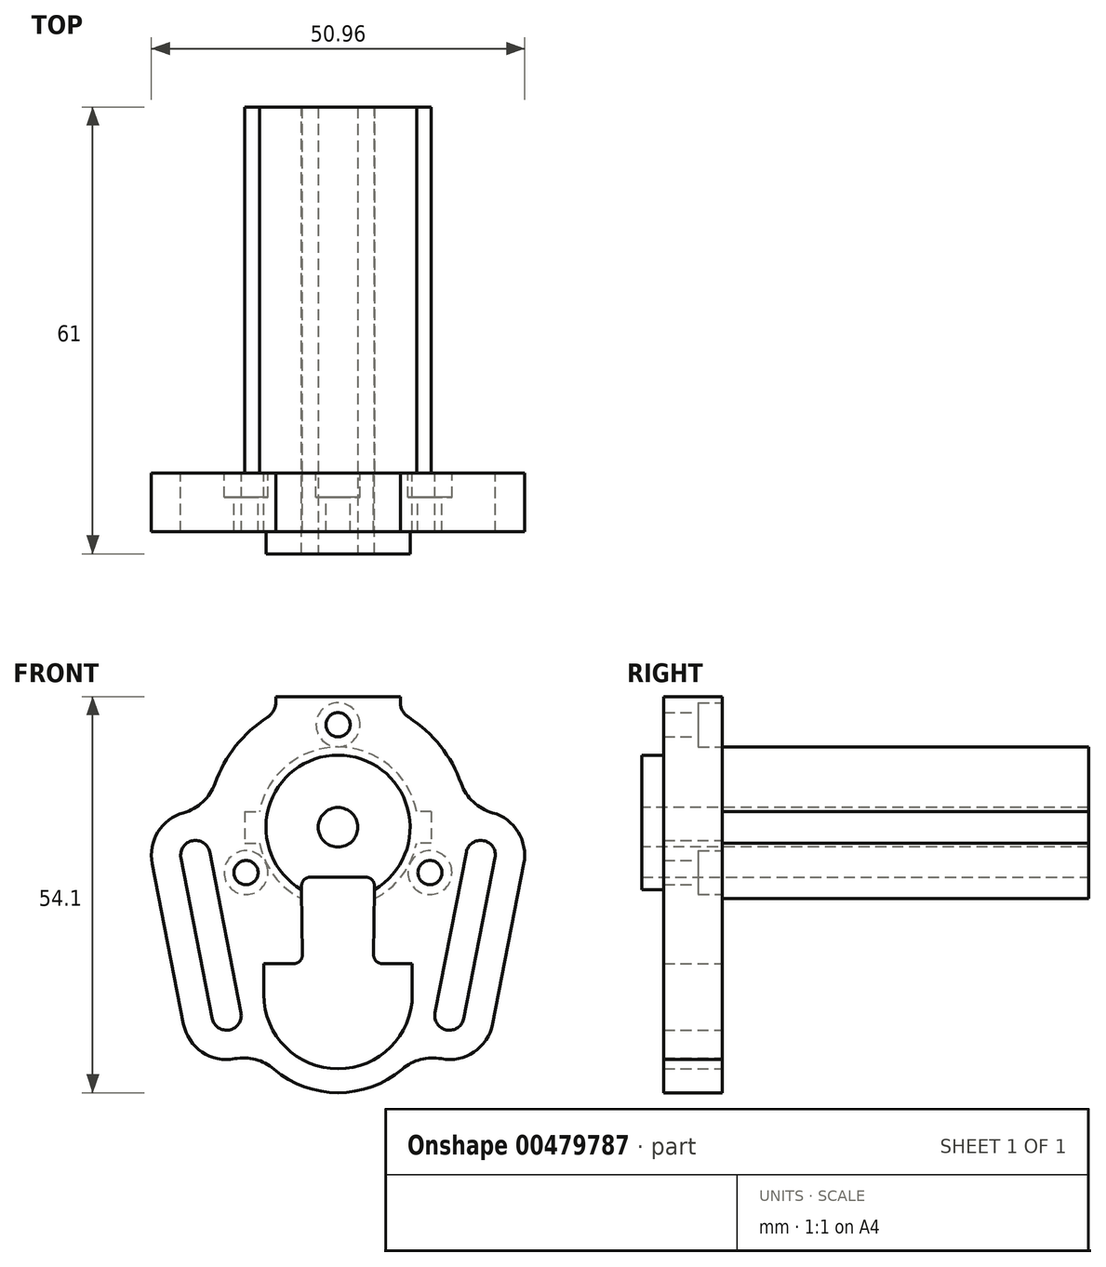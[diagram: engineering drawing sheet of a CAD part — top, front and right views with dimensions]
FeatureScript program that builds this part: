
annotation { "Feature Type Name" : "Feature", "Feature Type Description" : "" }
export const myFeature = defineFeature(function(context is Context, id is Id, definition is map)
    precondition{}
    {
        {
            var Q0;
            Q0=qCreatedBy(makeId("Front.planeOp"),FACE);
            var sketch = newSketch(context, id + "F0", { "sketchPlane" : qUnion([Q0])});
            skArc(sketch, "E0", {"start": v(16.82, 5.97) * mm, "mid": v(13.99, 11.1) * mm, "end": v(9.65, 15.02) * mm});
            skLineSegment(sketch, "E1", {"start": v(0, 17.85) * mm, "end": v(0, -22.75) * mm, "construction": true});
            skArc(sketch, "E2", {"start": v(-8.77, -33.02) * mm, "mid": v(0, -36.25) * mm, "end": v(8.77, -33.02) * mm});
            skLineSegment(sketch, "E3", {"start": v(13.25, -25.33) * mm, "end": v(17.52, -3.41) * mm});
            skLineSegment(sketch, "E4", {"start": v(-17.52, -3.41) * mm, "end": v(-13.25, -25.33) * mm});
            skArc(sketch, "E5", {"start": v(-17.52, -3.41) * mm, "mid": v(-19.87, -1.83) * mm, "end": v(-21.45, -4.18) * mm});
            skArc(sketch, "E6", {"start": v(-13.25, -25.33) * mm, "mid": v(-14.83, -27.68) * mm, "end": v(-17.18, -26.1) * mm});
            skArc(sketch, "E7", {"start": v(13.25, -25.33) * mm, "mid": v(14.83, -27.68) * mm, "end": v(17.18, -26.1) * mm});
            skArc(sketch, "E8", {"start": v(17.52, -3.41) * mm, "mid": v(19.87, -1.83) * mm, "end": v(21.45, -4.18) * mm});
            skLineSegment(sketch, "E9", {"start": v(17.18, -26.1) * mm, "end": v(21.45, -4.18) * mm});
            skLineSegment(sketch, "E10", {"start": v(-21.45, -4.18) * mm, "end": v(-17.18, -26.1) * mm});
            skArc(sketch, "E11.0", {"start": v(-14.09, -31.6) * mm, "mid": v(-18.58, -30.68) * mm, "end": v(-21.1, -26.86) * mm});
            skLineSegment(sketch, "E11.1", {"start": v(-25.37, -4.94) * mm, "end": v(-21.1, -26.86) * mm});
            skArc(sketch, "E11.2", {"start": v(-21.1, 1.98) * mm, "mid": v(-24.59, -0.64) * mm, "end": v(-25.37, -4.94) * mm});
            skArc(sketch, "E12.0", {"start": v(14.09, -31.6) * mm, "mid": v(18.58, -30.68) * mm, "end": v(21.1, -26.86) * mm});
            skLineSegment(sketch, "E12.1", {"start": v(21.1, -26.86) * mm, "end": v(25.37, -4.94) * mm});
            skArc(sketch, "E12.2", {"start": v(21.1, 1.98) * mm, "mid": v(24.59, -0.64) * mm, "end": v(25.37, -4.94) * mm});
            skPoint(sketch, "E13.visualSharp", {"position": v(-17.74, 1.95) * mm});
            skArc(sketch, "E13.filletArc", {"start": v(-21.1, 1.98) * mm, "mid": v(-18.47, 3.46) * mm, "end": v(-16.82, 5.97) * mm});
            skPoint(sketch, "E14.visualSharp", {"position": v(17.74, 1.95) * mm});
            skArc(sketch, "E14.filletArc", {"start": v(16.82, 5.97) * mm, "mid": v(18.47, 3.46) * mm, "end": v(21.1, 1.98) * mm});
            skPoint(sketch, "E15.visualSharp", {"position": v(-11.25, -30.22) * mm});
            skArc(sketch, "E15.filletArc", {"start": v(-8.77, -33.02) * mm, "mid": v(-11.27, -31.7) * mm, "end": v(-14.09, -31.6) * mm});
            skPoint(sketch, "E16.visualSharp", {"position": v(11.25, -30.22) * mm});
            skArc(sketch, "E16.filletArc", {"start": v(14.09, -31.6) * mm, "mid": v(11.27, -31.7) * mm, "end": v(8.77, -33.02) * mm});
            skLineSegment(sketch, "E17", {"start": v(0, 17.85) * mm, "end": v(-8.5, 17.85) * mm});
            skLineSegment(sketch, "E18.MirrorCS", {"start": v(0, 17.85) * mm, "end": v(8.5, 17.85) * mm});
            skLineSegment(sketch, "E19", {"start": v(-8.5, 17.85) * mm, "end": v(-8.5, 17.12) * mm});
            skLineSegment(sketch, "E20", {"start": v(8.5, 17.85) * mm, "end": v(8.5, 17.12) * mm});
            skArc(sketch, "E21.trimOffspring", {"start": v(-9.65, 15.02) * mm, "mid": v(-13.99, 11.1) * mm, "end": v(-16.82, 5.97) * mm});
            skPoint(sketch, "E22.visualSharp", {"position": v(-8.5, 15.7) * mm});
            skArc(sketch, "E22.filletArc", {"start": v(-9.65, 15.02) * mm, "mid": v(-8.8, 15.92) * mm, "end": v(-8.5, 17.12) * mm});
            skPoint(sketch, "E23.visualSharp", {"position": v(8.5, 15.7) * mm});
            skArc(sketch, "E23.filletArc", {"start": v(8.5, 17.12) * mm, "mid": v(8.8, 15.92) * mm, "end": v(9.65, 15.02) * mm});
            skSolve(sketch);
        }
        {
            var Q0;
            Q0=makeQuery(id+"F0.imprint","IMPRINT",FACE,{"disambiguationData":[TD([[makeQuery(id+"F0.imprint","IMPRINT",EDGE,{"derivedFrom":sQuery(id+"F0.wireOp",EDGE,"E0")}),1.0]])]});
            extrude(context, id + "F1", {"entities" : qUnion([Q0]), "depth" : 8 * mm});
        }
        {
            var Q0;
            Q0=makeQuery(id+"F1.opExtrude","CAP_FACE",FACE,{"disambiguationData":[OSD([sQuery(id+"F0.wireOp",EDGE,"E0"),sQuery(id+"F0.wireOp",EDGE,"E2"),sQuery(id+"F0.wireOp",EDGE,"E3"),sQuery(id+"F0.wireOp",EDGE,"E4"),sQuery(id+"F0.wireOp",EDGE,"E5"),sQuery(id+"F0.wireOp",EDGE,"E6"),sQuery(id+"F0.wireOp",EDGE,"E7"),sQuery(id+"F0.wireOp",EDGE,"E8"),sQuery(id+"F0.wireOp",EDGE,"E9"),sQuery(id+"F0.wireOp",EDGE,"E10"),sQuery(id+"F0.wireOp",EDGE,"E11.0"),sQuery(id+"F0.wireOp",EDGE,"E11.1"),sQuery(id+"F0.wireOp",EDGE,"E11.2"),sQuery(id+"F0.wireOp",EDGE,"E12.0"),sQuery(id+"F0.wireOp",EDGE,"E12.1"),sQuery(id+"F0.wireOp",EDGE,"E12.2"),sQuery(id+"F0.wireOp",EDGE,"E13.filletArc"),sQuery(id+"F0.wireOp",EDGE,"E14.filletArc"),sQuery(id+"F0.wireOp",EDGE,"E15.filletArc"),sQuery(id+"F0.wireOp",EDGE,"E16.filletArc"),sQuery(id+"F0.wireOp",EDGE,"E17"),sQuery(id+"F0.wireOp",EDGE,"E18.MirrorCS"),sQuery(id+"F0.wireOp",EDGE,"E19"),sQuery(id+"F0.wireOp",EDGE,"E20"),sQuery(id+"F0.wireOp",EDGE,"E21.trimOffspring"),sQuery(id+"F0.wireOp",EDGE,"E22.filletArc"),sQuery(id+"F0.wireOp",EDGE,"E23.filletArc")])],"isStart":false});
            var sketch = newSketch(context, id + "F2", { "sketchPlane" : qUnion([Q0])});
            skCircle(sketch, "E24", {"center": v(0, 0) * mm, "radius": 9.85 * mm});
            skSolve(sketch);
        }
        {
            var Q0;
            Q0=makeQuery(id+"F2.imprint","IMPRINT",FACE,{"disambiguationData":[TD([[makeQuery(id+"F2.imprint","IMPRINT",EDGE,{"derivedFrom":sQuery(id+"F2.wireOp",EDGE,"E24")}),1.0]])]});
            extrude(context, id + "F3", {"entities" : qUnion([Q0]), "operationType" : NewBodyOperationType.ADD, "depth" : 3 * mm});
        }
        {
            var Q0;
            Q0=makeQuery(id+"F1.opExtrude","CAP_FACE",FACE,{"disambiguationData":[OSD([sQuery(id+"F0.wireOp",EDGE,"E0"),sQuery(id+"F0.wireOp",EDGE,"E2"),sQuery(id+"F0.wireOp",EDGE,"E3"),sQuery(id+"F0.wireOp",EDGE,"E4"),sQuery(id+"F0.wireOp",EDGE,"E5"),sQuery(id+"F0.wireOp",EDGE,"E6"),sQuery(id+"F0.wireOp",EDGE,"E7"),sQuery(id+"F0.wireOp",EDGE,"E8"),sQuery(id+"F0.wireOp",EDGE,"E9"),sQuery(id+"F0.wireOp",EDGE,"E10"),sQuery(id+"F0.wireOp",EDGE,"E11.0"),sQuery(id+"F0.wireOp",EDGE,"E11.1"),sQuery(id+"F0.wireOp",EDGE,"E11.2"),sQuery(id+"F0.wireOp",EDGE,"E12.0"),sQuery(id+"F0.wireOp",EDGE,"E12.1"),sQuery(id+"F0.wireOp",EDGE,"E12.2"),sQuery(id+"F0.wireOp",EDGE,"E13.filletArc"),sQuery(id+"F0.wireOp",EDGE,"E14.filletArc"),sQuery(id+"F0.wireOp",EDGE,"E15.filletArc"),sQuery(id+"F0.wireOp",EDGE,"E16.filletArc"),sQuery(id+"F0.wireOp",EDGE,"E17"),sQuery(id+"F0.wireOp",EDGE,"E18.MirrorCS"),sQuery(id+"F0.wireOp",EDGE,"E19"),sQuery(id+"F0.wireOp",EDGE,"E20"),sQuery(id+"F0.wireOp",EDGE,"E21.trimOffspring"),sQuery(id+"F0.wireOp",EDGE,"E22.filletArc"),sQuery(id+"F0.wireOp",EDGE,"E23.filletArc")])],"isStart":true});
            var sketch = newSketch(context, id + "F4", { "sketchPlane" : qUnion([Q0])});
            skLineSegment(sketch, "E25", {"start": v(0, 0) * mm, "end": v(0, 2.17) * mm, "construction": true});
            skLineSegment(sketch, "E26", {"start": v(0, 2.17) * mm, "end": v(12.73, 2.17) * mm, "construction": true});
            skLineSegment(sketch, "E27.MirrorCS", {"start": v(0, 2.17) * mm, "end": v(-12.73, 2.17) * mm, "construction": true});
            skArc(sketch, "E28", {"start": v(-10.73, -2.17) * mm, "mid": v(0, -10.95) * mm, "end": v(10.73, -2.17) * mm});
            skLineSegment(sketch, "E29", {"start": v(-12.73, 2.17) * mm, "end": v(-10.73, 2.17) * mm});
            skLineSegment(sketch, "E30", {"start": v(-12.73, 2.17) * mm, "end": v(-12.73, -2.17) * mm});
            skLineSegment(sketch, "E31", {"start": v(0, 0) * mm, "end": v(4.4, 0) * mm, "construction": true});
            skLineSegment(sketch, "E32.MirrorCS", {"start": v(-12.73, -2.17) * mm, "end": v(-10.73, -2.17) * mm});
            skLineSegment(sketch, "E33.MirrorCS", {"start": v(12.73, -2.17) * mm, "end": v(10.73, -2.17) * mm});
            skLineSegment(sketch, "E34.MirrorCS", {"start": v(12.73, 2.17) * mm, "end": v(12.73, -2.17) * mm});
            skLineSegment(sketch, "E35.MirrorCS", {"start": v(12.73, 2.17) * mm, "end": v(10.73, 2.17) * mm});
            skArc(sketch, "E36.trimOffspring", {"start": v(10.73, 2.17) * mm, "mid": v(0, 10.95) * mm, "end": v(-10.73, 2.17) * mm});
            skSolve(sketch);
        }
        {
            var Q0;
            Q0 = qSketchRegion(id + "F4", true);
            extrude(context, id + "F5", {"entities" : qUnion([Q0]), "operationType" : NewBodyOperationType.ADD, "depth" : 50 * mm});
        }
        {
            var Q0;
            Q0=makeQuery(id+"F3.opExtrude","CAP_FACE",FACE,{"disambiguationData":[OSD([sQuery(id+"F2.wireOp",EDGE,"E24")])],"isStart":false});
            var sketch = newSketch(context, id + "F6", { "sketchPlane" : qUnion([Q0])});
            skCircle(sketch, "E37", {"center": v(0, 0) * mm, "radius": 2.7 * mm});
            skSolve(sketch);
        }
        {
            var Q0;
            Q0 = qSketchRegion(id + "F6", true);
            var Q1;
            Q1=makeQuery(id+"F6.imprint","IMPRINT",FACE,{"disambiguationData":[TD([[makeQuery(id+"F6.imprint","IMPRINT",EDGE,{"derivedFrom":sQuery(id+"F6.wireOp",EDGE,"E37")}),1.0]])]});
            extrude(context, id + "F7", {"entities" : qUnion([Q0, Q1]), "operationType" : NewBodyOperationType.REMOVE, "endBound" : BoundingType.UP_TO_NEXT, "oppositeDirection" : true, "depth" : 25 * mm});
        }
        {
            var Q0;
            Q0=makeQuery(id+"F4.imprint","IMPRINT",FACE,{"disambiguationData":[TD([[makeQuery(id+"F4.imprint","IMPRINT",EDGE,{"derivedFrom":sQuery(id+"F4.wireOp",EDGE,"E28")}),-1.0]])]});
            var sketch = newSketch(context, id + "F8", { "sketchPlane" : qUnion([Q0])});
            skCircle(sketch, "E38", {"center": v(0, 0) * mm, "radius": 14 * mm, "construction": true});
            skLineSegment(sketch, "E39", {"start": v(0, 0) * mm, "end": v(0, 22.33) * mm, "construction": true});
            skLineSegment(sketch, "E40", {"start": v(0, 0) * mm, "end": v(-15.1, -7.44) * mm, "construction": true});
            skLineSegment(sketch, "E41.MirrorCS", {"start": v(0, 0) * mm, "end": v(15.1, -7.44) * mm, "construction": true});
            skCircle(sketch, "E42", {"center": v(0, 14) * mm, "radius": 1.65 * mm});
            skCircle(sketch, "E43", {"center": v(-12.56, -6.2) * mm, "radius": 1.65 * mm});
            skCircle(sketch, "E44", {"center": v(12.56, -6.2) * mm, "radius": 1.65 * mm});
            skCircle(sketch, "E45", {"center": v(0, 14) * mm, "radius": 3 * mm});
            skCircle(sketch, "E46", {"center": v(-12.56, -6.2) * mm, "radius": 3 * mm});
            skCircle(sketch, "E47", {"center": v(12.56, -6.2) * mm, "radius": 3 * mm});
            skSolve(sketch);
        }
        {
            var Q0;
            Q0 = qSketchRegion(id + "F8", true);
            extrude(context, id + "F9", {"entities" : qUnion([Q0]), "operationType" : NewBodyOperationType.REMOVE, "oppositeDirection" : true, "depth" : 3.3 * mm});
        }
        {
            var Q0;
            Q0=makeQuery(id+"F9.boolean.opBoolean","SPLIT",FACE,{"disambiguationData":[TD([makeQuery(id+"F9.opExtrude","SWEPT_FACE",FACE,{"disambiguationData":[OSD([sQuery(id+"F8.wireOp",EDGE,"E44")])]})])],"derivedFrom":makeQuery(id+"F1.opExtrude","CAP_FACE",FACE,{"disambiguationData":[OSD([sQuery(id+"F0.wireOp",EDGE,"E0"),sQuery(id+"F0.wireOp",EDGE,"E2"),sQuery(id+"F0.wireOp",EDGE,"E3"),sQuery(id+"F0.wireOp",EDGE,"E4"),sQuery(id+"F0.wireOp",EDGE,"E5"),sQuery(id+"F0.wireOp",EDGE,"E6"),sQuery(id+"F0.wireOp",EDGE,"E7"),sQuery(id+"F0.wireOp",EDGE,"E8"),sQuery(id+"F0.wireOp",EDGE,"E9"),sQuery(id+"F0.wireOp",EDGE,"E10"),sQuery(id+"F0.wireOp",EDGE,"E11.0"),sQuery(id+"F0.wireOp",EDGE,"E11.1"),sQuery(id+"F0.wireOp",EDGE,"E11.2"),sQuery(id+"F0.wireOp",EDGE,"E12.0"),sQuery(id+"F0.wireOp",EDGE,"E12.1"),sQuery(id+"F0.wireOp",EDGE,"E12.2"),sQuery(id+"F0.wireOp",EDGE,"E13.filletArc"),sQuery(id+"F0.wireOp",EDGE,"E14.filletArc"),sQuery(id+"F0.wireOp",EDGE,"E15.filletArc"),sQuery(id+"F0.wireOp",EDGE,"E16.filletArc"),sQuery(id+"F0.wireOp",EDGE,"E17"),sQuery(id+"F0.wireOp",EDGE,"E18.MirrorCS"),sQuery(id+"F0.wireOp",EDGE,"E19"),sQuery(id+"F0.wireOp",EDGE,"E20"),sQuery(id+"F0.wireOp",EDGE,"E21.trimOffspring"),sQuery(id+"F0.wireOp",EDGE,"E22.filletArc"),sQuery(id+"F0.wireOp",EDGE,"E23.filletArc")])],"isStart":true})});
            extrude(context, id + "F10", {"entities" : qUnion([Q0]), "operationType" : NewBodyOperationType.REMOVE, "oppositeDirection" : true, "depth" : 25 * mm});
        }
        {
            var Q0;
            Q0=makeQuery(id+"F9.boolean.opBoolean","SPLIT",FACE,{"disambiguationData":[TD([makeQuery(id+"F9.opExtrude","SWEPT_FACE",FACE,{"disambiguationData":[OSD([sQuery(id+"F8.wireOp",EDGE,"E42")])]})])],"derivedFrom":makeQuery(id+"F1.opExtrude","CAP_FACE",FACE,{"disambiguationData":[OSD([sQuery(id+"F0.wireOp",EDGE,"E0"),sQuery(id+"F0.wireOp",EDGE,"E2"),sQuery(id+"F0.wireOp",EDGE,"E3"),sQuery(id+"F0.wireOp",EDGE,"E4"),sQuery(id+"F0.wireOp",EDGE,"E5"),sQuery(id+"F0.wireOp",EDGE,"E6"),sQuery(id+"F0.wireOp",EDGE,"E7"),sQuery(id+"F0.wireOp",EDGE,"E8"),sQuery(id+"F0.wireOp",EDGE,"E9"),sQuery(id+"F0.wireOp",EDGE,"E10"),sQuery(id+"F0.wireOp",EDGE,"E11.0"),sQuery(id+"F0.wireOp",EDGE,"E11.1"),sQuery(id+"F0.wireOp",EDGE,"E11.2"),sQuery(id+"F0.wireOp",EDGE,"E12.0"),sQuery(id+"F0.wireOp",EDGE,"E12.1"),sQuery(id+"F0.wireOp",EDGE,"E12.2"),sQuery(id+"F0.wireOp",EDGE,"E13.filletArc"),sQuery(id+"F0.wireOp",EDGE,"E14.filletArc"),sQuery(id+"F0.wireOp",EDGE,"E15.filletArc"),sQuery(id+"F0.wireOp",EDGE,"E16.filletArc"),sQuery(id+"F0.wireOp",EDGE,"E17"),sQuery(id+"F0.wireOp",EDGE,"E18.MirrorCS"),sQuery(id+"F0.wireOp",EDGE,"E19"),sQuery(id+"F0.wireOp",EDGE,"E20"),sQuery(id+"F0.wireOp",EDGE,"E21.trimOffspring"),sQuery(id+"F0.wireOp",EDGE,"E22.filletArc"),sQuery(id+"F0.wireOp",EDGE,"E23.filletArc")])],"isStart":true})});
            extrude(context, id + "F11", {"entities" : qUnion([Q0]), "operationType" : NewBodyOperationType.REMOVE, "oppositeDirection" : true, "depth" : 25 * mm});
        }
        {
            var Q0;
            Q0=makeQuery(id+"F9.boolean.opBoolean","SPLIT",FACE,{"disambiguationData":[TD([makeQuery(id+"F9.opExtrude","SWEPT_FACE",FACE,{"disambiguationData":[OSD([sQuery(id+"F8.wireOp",EDGE,"E43")])]})])],"derivedFrom":makeQuery(id+"F1.opExtrude","CAP_FACE",FACE,{"disambiguationData":[OSD([sQuery(id+"F0.wireOp",EDGE,"E0"),sQuery(id+"F0.wireOp",EDGE,"E2"),sQuery(id+"F0.wireOp",EDGE,"E3"),sQuery(id+"F0.wireOp",EDGE,"E4"),sQuery(id+"F0.wireOp",EDGE,"E5"),sQuery(id+"F0.wireOp",EDGE,"E6"),sQuery(id+"F0.wireOp",EDGE,"E7"),sQuery(id+"F0.wireOp",EDGE,"E8"),sQuery(id+"F0.wireOp",EDGE,"E9"),sQuery(id+"F0.wireOp",EDGE,"E10"),sQuery(id+"F0.wireOp",EDGE,"E11.0"),sQuery(id+"F0.wireOp",EDGE,"E11.1"),sQuery(id+"F0.wireOp",EDGE,"E11.2"),sQuery(id+"F0.wireOp",EDGE,"E12.0"),sQuery(id+"F0.wireOp",EDGE,"E12.1"),sQuery(id+"F0.wireOp",EDGE,"E12.2"),sQuery(id+"F0.wireOp",EDGE,"E13.filletArc"),sQuery(id+"F0.wireOp",EDGE,"E14.filletArc"),sQuery(id+"F0.wireOp",EDGE,"E15.filletArc"),sQuery(id+"F0.wireOp",EDGE,"E16.filletArc"),sQuery(id+"F0.wireOp",EDGE,"E17"),sQuery(id+"F0.wireOp",EDGE,"E18.MirrorCS"),sQuery(id+"F0.wireOp",EDGE,"E19"),sQuery(id+"F0.wireOp",EDGE,"E20"),sQuery(id+"F0.wireOp",EDGE,"E21.trimOffspring"),sQuery(id+"F0.wireOp",EDGE,"E22.filletArc"),sQuery(id+"F0.wireOp",EDGE,"E23.filletArc")])],"isStart":true})});
            extrude(context, id + "F12", {"entities" : qUnion([Q0]), "operationType" : NewBodyOperationType.REMOVE, "oppositeDirection" : true, "depth" : 25 * mm});
        }
        {
            var Q0;
            Q0=qCreatedBy(makeId("Front.planeOp"),FACE);
            cPlane(context, id + "F13", {"entities" : qUnion([Q0]), "cplaneType" : CPlaneType.OFFSET, "offset" : 50 * mm, "oppositeDirection" : true, "width" : 150 * mm, "height" : 150 * mm});
        }
        {
            var Q0;
            Q0=qCreatedBy(id+"F13.planeOp",FACE);
            var sketch = newSketch(context, id + "F14", { "sketchPlane" : qUnion([Q0])});
            skLineSegment(sketch, "E48", {"start": v(-6.06, -18.62) * mm, "end": v(-10.14, -18.62) * mm});
            skLineSegment(sketch, "E49.MirrorCS", {"start": v(6.06, -18.62) * mm, "end": v(10.14, -18.62) * mm});
            skArc(sketch, "E50", {"start": v(-10.14, -22.84) * mm, "mid": v(0, -32.98) * mm, "end": v(10.14, -22.84) * mm});
            skLineSegment(sketch, "E51", {"start": v(-10.14, -18.62) * mm, "end": v(-10.14, -22.84) * mm});
            skLineSegment(sketch, "E52", {"start": v(10.14, -18.62) * mm, "end": v(10.14, -22.84) * mm});
            skLineSegment(sketch, "E53", {"start": v(-4.98, -8.03) * mm, "end": v(-4.86, -17.4) * mm});
            skLineSegment(sketch, "E54.MirrorCS", {"start": v(4.98, -8.03) * mm, "end": v(4.86, -17.4) * mm});
            skLineSegment(sketch, "E55", {"start": v(3.78, -6.82) * mm, "end": v(-3.78, -6.82) * mm});
            skLineSegment(sketch, "E56", {"start": v(0, 0) * mm, "end": v(0, -22.84) * mm});
            skLineSegment(sketch, "E57", {"start": v(0, 0) * mm, "end": v(0, -6.82) * mm});
            skPoint(sketch, "E58.visualSharp", {"position": v(5, -6.82) * mm});
            skArc(sketch, "E58.filletArc", {"start": v(4.98, -8.03) * mm, "mid": v(4.64, -7.18) * mm, "end": v(3.78, -6.82) * mm});
            skPoint(sketch, "E59.visualSharp", {"position": v(-5, -6.82) * mm});
            skArc(sketch, "E59.filletArc", {"start": v(-3.78, -6.82) * mm, "mid": v(-4.64, -7.18) * mm, "end": v(-4.98, -8.03) * mm});
            skPoint(sketch, "E60.visualSharp", {"position": v(4.84, -18.62) * mm});
            skArc(sketch, "E60.filletArc", {"start": v(4.86, -17.4) * mm, "mid": v(5.2, -18.26) * mm, "end": v(6.06, -18.62) * mm});
            skPoint(sketch, "E61.visualSharp", {"position": v(-4.84, -18.62) * mm});
            skArc(sketch, "E61.filletArc", {"start": v(-6.06, -18.62) * mm, "mid": v(-5.2, -18.26) * mm, "end": v(-4.86, -17.4) * mm});
            skSolve(sketch);
        }
        {
            var Q0;
            Q0=makeQuery(id+"F14.imprint","IMPRINT",FACE,{"disambiguationData":[TD([[makeQuery(id+"F14.imprint","IMPRINT",EDGE,{"derivedFrom":sQuery(id+"F14.wireOp",EDGE,"E48")}),1.0]])]});
            extrude(context, id + "F15", {"entities" : qUnion([Q0]), "operationType" : NewBodyOperationType.REMOVE, "endBound" : BoundingType.THROUGH_ALL, "depth" : 25 * mm});
        }
    });
